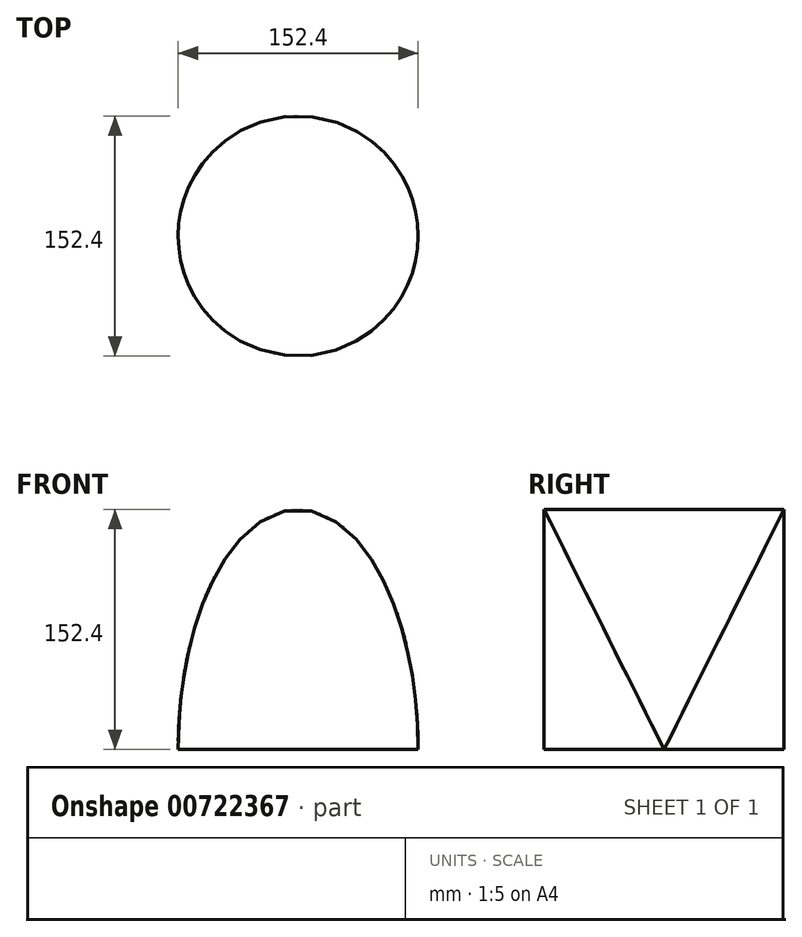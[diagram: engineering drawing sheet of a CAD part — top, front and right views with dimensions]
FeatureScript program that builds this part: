
annotation { "Feature Type Name" : "Feature", "Feature Type Description" : "" }
export const myFeature = defineFeature(function(context is Context, id is Id, definition is map)
    precondition{}
    {
        {
            var Q0;
            Q0=qCreatedBy(makeId("Front.planeOp"),FACE);
            var sketch = newSketch(context, id + "F0", { "sketchPlane" : qUnion([Q0])});
            skEllipse(sketch, "E0", {"center": v(0, 0) * mm, "majorRadius": 152.4 * mm, "minorRadius": 76.2 * mm, "majorAxis": v(0, 1)});
            skSolve(sketch);
        }
        {
            var Q0;
            Q0=qCreatedBy(makeId("Top.planeOp"),FACE);
            var sketch = newSketch(context, id + "F1", { "sketchPlane" : qUnion([Q0])});
            skCircle(sketch, "E1", {"center": v(0, 0) * mm, "radius": 76.2 * mm});
            skSolve(sketch);
        }
        {
            var Q0;
            Q0=makeQuery(id+"F1.imprint","IMPRINT",FACE,{"disambiguationData":[TD([[makeQuery(id+"F1.imprint","IMPRINT",EDGE,{"derivedFrom":sQuery(id+"F1.wireOp",EDGE,"E1")}),1.0]])]});
            extrude(context, id + "F2", {"entities" : qUnion([Q0]), "depth" : 152.4 * mm, "offsetDistance" : 25.4 * mm});
        }
        {
            var Q0;
            Q0=qCreatedBy(makeId("Top.planeOp"),FACE);
            var sketch = newSketch(context, id + "F3", { "sketchPlane" : qUnion([Q0])});
            skLineSegment(sketch, "E2.bottom", {"start": v(76.2, -76.2) * mm, "end": v(152.4, -76.2) * mm});
            skLineSegment(sketch, "E2.top", {"start": v(76.2, 76.2) * mm, "end": v(152.4, 76.2) * mm});
            skLineSegment(sketch, "E2.left", {"start": v(76.2, -76.2) * mm, "end": v(76.2, 76.2) * mm});
            skLineSegment(sketch, "E2.right", {"start": v(152.4, -76.2) * mm, "end": v(152.4, 76.2) * mm});
            skPoint(sketch, "E2.middle", {"position": v(114.3, 0) * mm});
            skSolve(sketch);
        }
        {
            var Q0;
            Q0=makeQuery(id+"F3.imprint","IMPRINT",FACE,{"disambiguationData":[TD([[makeQuery(id+"F3.imprint","IMPRINT",EDGE,{"derivedFrom":sQuery(id+"F3.wireOp",EDGE,"E2.bottom")}),1.0]])]});
            var Q1;
            Q1=sQuery(id+"F0.wireOp",EDGE,"E0");
            sweep(context, id + "F4", {"operationType" : NewBodyOperationType.REMOVE, "profiles" : qUnion([Q0]), "path" : qUnion([Q1])});
        }
    });
